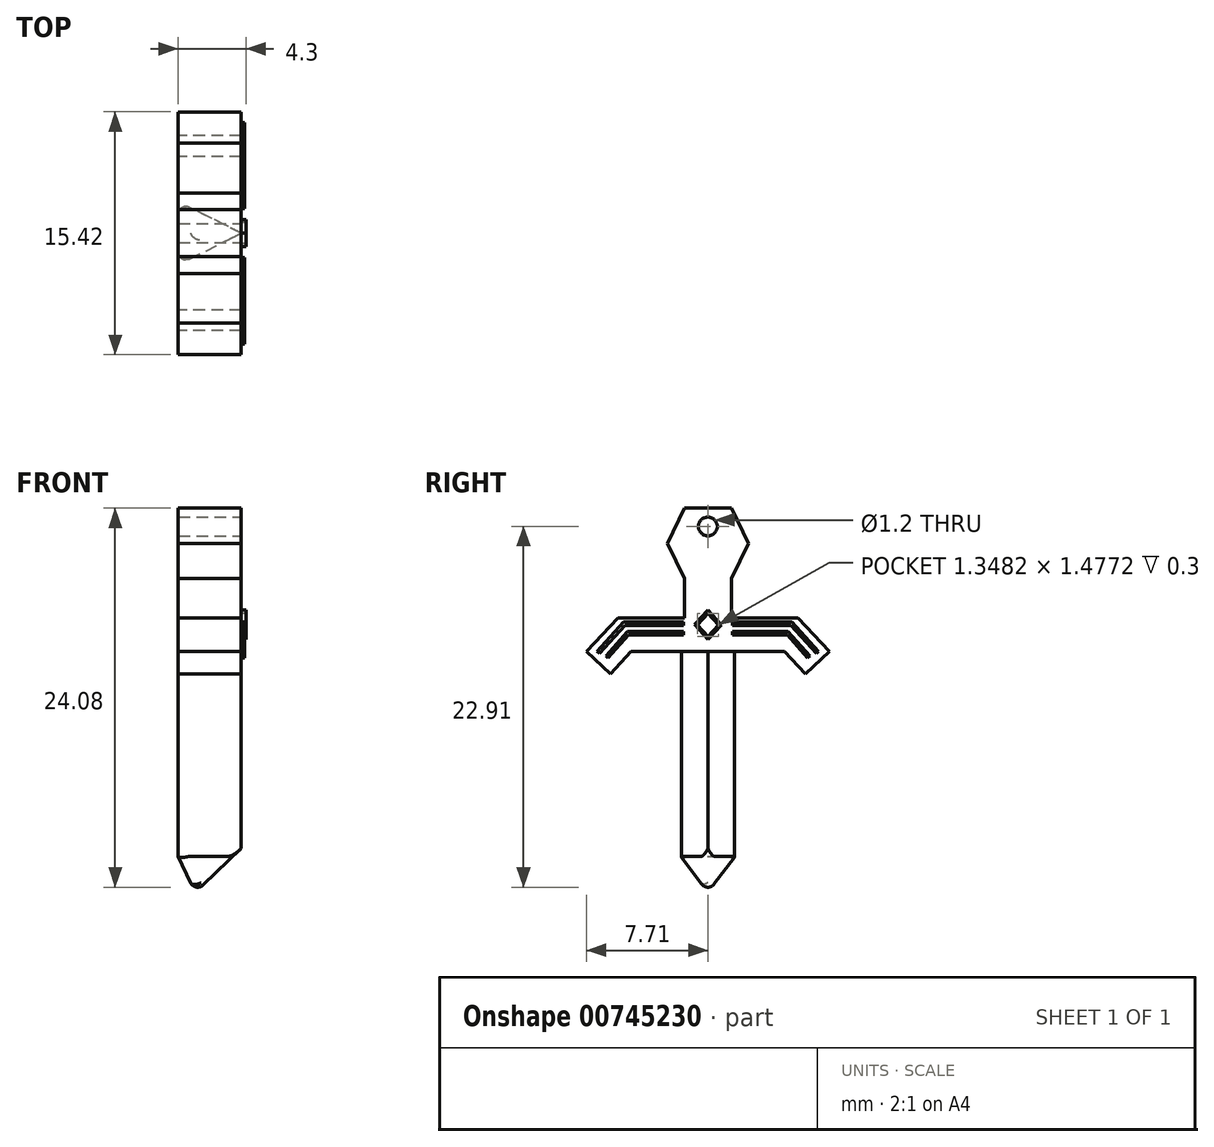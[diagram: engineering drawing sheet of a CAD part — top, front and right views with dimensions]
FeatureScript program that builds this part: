
annotation { "Feature Type Name" : "Feature", "Feature Type Description" : "" }
export const myFeature = defineFeature(function(context is Context, id is Id, definition is map)
    precondition{}
    {
        {
            var Q0;
            Q0=qCreatedBy(makeId("Right.planeOp"),FACE);
            var sketch = newSketch(context, id + "F0", { "sketchPlane" : qUnion([Q0])});
            skLineSegment(sketch, "E0", {"start": v(-3.3, 24.4) * mm, "end": v(1.49, 24.4) * mm});
            skLineSegment(sketch, "E1", {"start": v(1.49, 24.4) * mm, "end": v(2.56, 22.15) * mm});
            skLineSegment(sketch, "E2", {"start": v(2.56, 22.15) * mm, "end": v(1.49, 19.92) * mm});
            skLineSegment(sketch, "E3", {"start": v(1.49, 19.92) * mm, "end": v(1.49, 17.4) * mm});
            skLineSegment(sketch, "E4", {"start": v(1.49, 17.4) * mm, "end": v(5.72, 17.4) * mm});
            skLineSegment(sketch, "E5", {"start": v(5.72, 17.4) * mm, "end": v(7.7, 15.27) * mm});
            skLineSegment(sketch, "E6", {"start": v(7.7, 15.27) * mm, "end": v(6.2, 13.86) * mm});
            skLineSegment(sketch, "E7", {"start": v(6.2, 13.86) * mm, "end": v(4.87, 15.27) * mm});
            skLineSegment(sketch, "E8", {"start": v(4.87, 15.27) * mm, "end": v(1.49, 15.27) * mm});
            skLineSegment(sketch, "E9.MirrorCS", {"start": v(-1.49, 24.4) * mm, "end": v(-2.56, 22.15) * mm});
            skLineSegment(sketch, "E10.MirrorCS", {"start": v(-2.56, 22.15) * mm, "end": v(-1.49, 19.92) * mm});
            skLineSegment(sketch, "E11.MirrorCS", {"start": v(-1.49, 19.92) * mm, "end": v(-1.49, 17.4) * mm});
            skLineSegment(sketch, "E12.MirrorCS", {"start": v(-1.49, 17.4) * mm, "end": v(-5.72, 17.4) * mm});
            skLineSegment(sketch, "E13.MirrorCS", {"start": v(-5.72, 17.4) * mm, "end": v(-7.7, 15.27) * mm});
            skLineSegment(sketch, "E14.MirrorCS", {"start": v(-7.7, 15.27) * mm, "end": v(-6.2, 13.86) * mm});
            skLineSegment(sketch, "E15.MirrorCS", {"start": v(-6.2, 13.86) * mm, "end": v(-4.87, 15.27) * mm});
            skLineSegment(sketch, "E16.MirrorCS", {"start": v(-4.87, 15.27) * mm, "end": v(-1.49, 15.27) * mm});
            skLineSegment(sketch, "E17", {"start": v(-1.49, 15.27) * mm, "end": v(1.49, 15.27) * mm});
            skSolve(sketch);
        }
        {
            var Q0;
            Q0 = qSketchRegion(id + "F0", true);
            extrude(context, id + "F1", {"entities" : qUnion([Q0]), "depth" : 4 * mm, "offsetDistance" : 25 * mm});
        }
        {
            var Q0;
            Q0=makeQuery(id+"F1.opExtrude","SWEPT_FACE",FACE,{"disambiguationData":[OSD([sQuery(id+"F0.wireOp",EDGE,"E8"),sQuery(id+"F0.wireOp",EDGE,"E16.MirrorCS"),sQuery(id+"F0.wireOp",EDGE,"E17")])]});
            var sketch = newSketch(context, id + "F2", { "sketchPlane" : qUnion([Q0])});
            skLineSegment(sketch, "E18", {"start": v(0, 0) * mm, "end": v(0, 2) * mm});
            skLineSegment(sketch, "E19", {"start": v(0, 2) * mm, "end": v(4, 0) * mm});
            skLineSegment(sketch, "E20", {"start": v(4, 0) * mm, "end": v(0, -2) * mm});
            skLineSegment(sketch, "E21", {"start": v(0, -2) * mm, "end": v(0, 0) * mm});
            skSolve(sketch);
        }
        {
            var Q0;
            Q0=makeQuery(id+"F2.imprint","IMPRINT",FACE,{"disambiguationData":[TD([[makeQuery(id+"F2.imprint","IMPRINT",EDGE,{"derivedFrom":sQuery(id+"F2.wireOp",EDGE,"E18")}),1.0]])]});
            extrude(context, id + "F3", {"entities" : qUnion([Q0]), "operationType" : NewBodyOperationType.ADD, "depth" : 13 * mm, "offsetDistance" : 25 * mm});
        }
        {
            var Q0;
            Q0=makeQuery(id+"F1.opExtrude","CAP_FACE",FACE,{"disambiguationData":[OSD([sQuery(id+"F0.wireOp",EDGE,"E0"),sQuery(id+"F0.wireOp",EDGE,"E1"),sQuery(id+"F0.wireOp",EDGE,"E2"),sQuery(id+"F0.wireOp",EDGE,"E3"),sQuery(id+"F0.wireOp",EDGE,"E4"),sQuery(id+"F0.wireOp",EDGE,"E5"),sQuery(id+"F0.wireOp",EDGE,"E6"),sQuery(id+"F0.wireOp",EDGE,"E7"),sQuery(id+"F0.wireOp",EDGE,"E8"),sQuery(id+"F0.wireOp",EDGE,"E9.MirrorCS"),sQuery(id+"F0.wireOp",EDGE,"E10.MirrorCS"),sQuery(id+"F0.wireOp",EDGE,"E11.MirrorCS"),sQuery(id+"F0.wireOp",EDGE,"E12.MirrorCS"),sQuery(id+"F0.wireOp",EDGE,"E13.MirrorCS"),sQuery(id+"F0.wireOp",EDGE,"E14.MirrorCS"),sQuery(id+"F0.wireOp",EDGE,"E15.MirrorCS"),sQuery(id+"F0.wireOp",EDGE,"E16.MirrorCS"),sQuery(id+"F0.wireOp",EDGE,"E17")])],"isStart":false});
            var sketch = newSketch(context, id + "F4", { "sketchPlane" : qUnion([Q0])});
            skCircle(sketch, "E22", {"center": v(0, 23.22) * mm, "radius": 0.6 * mm});
            skSolve(sketch);
        }
        {
            var Q0;
            Q0=makeQuery(id+"F4.imprint","IMPRINT",FACE,{"disambiguationData":[TD([[makeQuery(id+"F4.imprint","IMPRINT",EDGE,{"derivedFrom":sQuery(id+"F4.wireOp",EDGE,"E22")}),1.0]])]});
            extrude(context, id + "F5", {"entities" : qUnion([Q0]), "operationType" : NewBodyOperationType.REMOVE, "oppositeDirection" : true, "depth" : 25 * mm, "offsetDistance" : 25 * mm});
        }
        {
            var Q0;
            Q0=makeQuery(id+"F3.opExtrude","CAP_FACE",FACE,{"disambiguationData":[OSD([sQuery(id+"F2.wireOp",EDGE,"E18"),sQuery(id+"F2.wireOp",EDGE,"E19"),sQuery(id+"F2.wireOp",EDGE,"E20"),sQuery(id+"F2.wireOp",EDGE,"E21")])],"isStart":false});
            var sketch = newSketch(context, id + "F6", { "sketchPlane" : qUnion([Q0])});
            skLineSegment(sketch, "E23", {"start": v(0, 0) * mm, "end": v(0, 2) * mm});
            skLineSegment(sketch, "E24", {"start": v(0, 2) * mm, "end": v(4, 0) * mm});
            skLineSegment(sketch, "E25", {"start": v(4, 0) * mm, "end": v(0, -2) * mm});
            skLineSegment(sketch, "E26", {"start": v(0, -2) * mm, "end": v(0, 0) * mm});
            skSolve(sketch);
        }
        {
            var Q0;
            Q0 = qSketchRegion(id + "F6", true);
            extrude(context, id + "F7", {"entities" : qUnion([Q0]), "operationType" : NewBodyOperationType.ADD, "depth" : 2.8 * mm, "offsetDistance" : 25 * mm, "hasDraft" : true, "draftAngle" : 25 * degree, "draftPullDirection" : true});
        }
        {
            var Q0;
            Q0=makeQuery(id+"F1.opExtrude","CAP_FACE",FACE,{"disambiguationData":[OSD([sQuery(id+"F0.wireOp",EDGE,"E0"),sQuery(id+"F0.wireOp",EDGE,"E1"),sQuery(id+"F0.wireOp",EDGE,"E2"),sQuery(id+"F0.wireOp",EDGE,"E3"),sQuery(id+"F0.wireOp",EDGE,"E4"),sQuery(id+"F0.wireOp",EDGE,"E5"),sQuery(id+"F0.wireOp",EDGE,"E6"),sQuery(id+"F0.wireOp",EDGE,"E7"),sQuery(id+"F0.wireOp",EDGE,"E8"),sQuery(id+"F0.wireOp",EDGE,"E9.MirrorCS"),sQuery(id+"F0.wireOp",EDGE,"E10.MirrorCS"),sQuery(id+"F0.wireOp",EDGE,"E11.MirrorCS"),sQuery(id+"F0.wireOp",EDGE,"E12.MirrorCS"),sQuery(id+"F0.wireOp",EDGE,"E13.MirrorCS"),sQuery(id+"F0.wireOp",EDGE,"E14.MirrorCS"),sQuery(id+"F0.wireOp",EDGE,"E15.MirrorCS"),sQuery(id+"F0.wireOp",EDGE,"E16.MirrorCS"),sQuery(id+"F0.wireOp",EDGE,"E17")])],"isStart":false});
            var sketch = newSketch(context, id + "F8", { "sketchPlane" : qUnion([Q0])});
            skLineSegment(sketch, "E27", {"start": v(-1.55, 17.02) * mm, "end": v(-1.55, 16.92) * mm});
            skLineSegment(sketch, "E28", {"start": v(-1.55, 16.92) * mm, "end": v(-5.28, 16.92) * mm});
            skLineSegment(sketch, "E29", {"start": v(-5.28, 16.92) * mm, "end": v(-6.88, 15.16) * mm});
            skLineSegment(sketch, "E30", {"start": v(-6.88, 15.16) * mm, "end": v(-7.03, 15.3) * mm});
            skLineSegment(sketch, "E31", {"start": v(-7.03, 15.3) * mm, "end": v(-5.35, 17.14) * mm});
            skLineSegment(sketch, "E32", {"start": v(-5.35, 17.14) * mm, "end": v(-1.55, 17.14) * mm});
            skLineSegment(sketch, "E33", {"start": v(-1.55, 17.14) * mm, "end": v(-1.55, 17.02) * mm});
            skLineSegment(sketch, "E34", {"start": v(-1.55, 16.46) * mm, "end": v(-1.55, 16.33) * mm});
            skLineSegment(sketch, "E35", {"start": v(-1.55, 16.33) * mm, "end": v(-5.05, 16.33) * mm});
            skLineSegment(sketch, "E36", {"start": v(-5.05, 16.33) * mm, "end": v(-6.34, 14.87) * mm});
            skLineSegment(sketch, "E37", {"start": v(-6.34, 14.87) * mm, "end": v(-6.47, 15) * mm});
            skLineSegment(sketch, "E38", {"start": v(-6.47, 15) * mm, "end": v(-5.1, 16.54) * mm});
            skLineSegment(sketch, "E39", {"start": v(-5.1, 16.54) * mm, "end": v(-1.55, 16.54) * mm});
            skLineSegment(sketch, "E40", {"start": v(-1.55, 16.54) * mm, "end": v(-1.55, 16.46) * mm});
            skLineSegment(sketch, "E41.MirrorCS", {"start": v(5.1, 16.54) * mm, "end": v(1.55, 16.54) * mm});
            skLineSegment(sketch, "E42.MirrorCS", {"start": v(1.55, 16.33) * mm, "end": v(5.05, 16.33) * mm});
            skLineSegment(sketch, "E43.MirrorCS", {"start": v(1.55, 16.46) * mm, "end": v(1.55, 16.33) * mm});
            skLineSegment(sketch, "E44.MirrorCS", {"start": v(1.55, 16.54) * mm, "end": v(1.55, 16.46) * mm});
            skLineSegment(sketch, "E45.MirrorCS", {"start": v(5.05, 16.33) * mm, "end": v(6.34, 14.87) * mm});
            skLineSegment(sketch, "E46.MirrorCS", {"start": v(6.47, 15) * mm, "end": v(5.1, 16.54) * mm});
            skLineSegment(sketch, "E47.MirrorCS", {"start": v(6.34, 14.87) * mm, "end": v(6.47, 15) * mm});
            skLineSegment(sketch, "E48.MirrorCS", {"start": v(6.88, 15.16) * mm, "end": v(7.03, 15.3) * mm});
            skLineSegment(sketch, "E49.MirrorCS", {"start": v(5.28, 16.92) * mm, "end": v(6.88, 15.16) * mm});
            skLineSegment(sketch, "E50.MirrorCS", {"start": v(7.03, 15.3) * mm, "end": v(5.35, 17.14) * mm});
            skLineSegment(sketch, "E51.MirrorCS", {"start": v(1.55, 16.92) * mm, "end": v(5.28, 16.92) * mm});
            skLineSegment(sketch, "E52.MirrorCS", {"start": v(5.35, 17.14) * mm, "end": v(1.55, 17.14) * mm});
            skLineSegment(sketch, "E53.MirrorCS", {"start": v(1.55, 17.14) * mm, "end": v(1.55, 17.02) * mm});
            skLineSegment(sketch, "E54.MirrorCS", {"start": v(1.55, 17.02) * mm, "end": v(1.55, 16.92) * mm});
            skSolve(sketch);
        }
        {
            var Q0;
            Q0 = qSketchRegion(id + "F8", true);
            extrude(context, id + "F9", {"entities" : qUnion([Q0]), "operationType" : NewBodyOperationType.ADD, "depth" : 0.2 * mm, "offsetDistance" : 25 * mm});
        }
        {
            var Q0;
            Q0=makeQuery(id+"F1.opExtrude","CAP_FACE",FACE,{"disambiguationData":[OSD([sQuery(id+"F0.wireOp",EDGE,"E0"),sQuery(id+"F0.wireOp",EDGE,"E1"),sQuery(id+"F0.wireOp",EDGE,"E2"),sQuery(id+"F0.wireOp",EDGE,"E3"),sQuery(id+"F0.wireOp",EDGE,"E4"),sQuery(id+"F0.wireOp",EDGE,"E5"),sQuery(id+"F0.wireOp",EDGE,"E6"),sQuery(id+"F0.wireOp",EDGE,"E7"),sQuery(id+"F0.wireOp",EDGE,"E8"),sQuery(id+"F0.wireOp",EDGE,"E9.MirrorCS"),sQuery(id+"F0.wireOp",EDGE,"E10.MirrorCS"),sQuery(id+"F0.wireOp",EDGE,"E11.MirrorCS"),sQuery(id+"F0.wireOp",EDGE,"E12.MirrorCS"),sQuery(id+"F0.wireOp",EDGE,"E13.MirrorCS"),sQuery(id+"F0.wireOp",EDGE,"E14.MirrorCS"),sQuery(id+"F0.wireOp",EDGE,"E15.MirrorCS"),sQuery(id+"F0.wireOp",EDGE,"E16.MirrorCS"),sQuery(id+"F0.wireOp",EDGE,"E17")])],"isStart":false});
            var sketch = newSketch(context, id + "F10", { "sketchPlane" : qUnion([Q0])});
            skLineSegment(sketch, "E55", {"start": v(0, 17.71) * mm, "end": v(-0.67, 16.97) * mm});
            skLineSegment(sketch, "E56", {"start": v(-0.67, 16.97) * mm, "end": v(0, 16.23) * mm});
            skLineSegment(sketch, "E57.MirrorCS", {"start": v(0, 17.71) * mm, "end": v(0.67, 16.97) * mm});
            skLineSegment(sketch, "E58.MirrorCS", {"start": v(0.67, 16.97) * mm, "end": v(0, 16.23) * mm});
            skLineSegment(sketch, "E59", {"start": v(0, 17.91) * mm, "end": v(-0.86, 17) * mm});
            skLineSegment(sketch, "E60", {"start": v(-0.86, 17) * mm, "end": v(0, 16.03) * mm});
            skLineSegment(sketch, "E61", {"start": v(0, 16.03) * mm, "end": v(0.86, 16.97) * mm});
            skLineSegment(sketch, "E62", {"start": v(0.86, 16.97) * mm, "end": v(0, 17.91) * mm});
            skSolve(sketch);
        }
        {
            var Q0;
            Q0 = qSketchRegion(id + "F10", true);
            extrude(context, id + "F11", {"entities" : qUnion([Q0]), "operationType" : NewBodyOperationType.ADD, "depth" : 0.3 * mm, "offsetDistance" : 25 * mm});
        }
        {
            var Q0;
            Q0=makeQuery(id+"F3.opExtrude","SWEPT_EDGE",EDGE,{"disambiguationData":[OSD([sQuery(id+"F0.wireOp",EDGE,"E8"),sQuery(id+"F0.wireOp",EDGE,"E16.MirrorCS"),sQuery(id+"F0.wireOp",EDGE,"E17"),sQuery(id+"F2.wireOp",EDGE,"E20"),sQuery(id+"F2.wireOp",EDGE,"E21")])]});
            fillet(context, id + "F12", {"entities" : qUnion([Q0]), "radius" : 0.5 * mm, "tangentPropagation" : true, "allowEdgeOverflow" : false});
        }
        {
            var Q0;
            Q0=makeQuery(id+"F3.opExtrude","SWEPT_EDGE",EDGE,{"disambiguationData":[OSD([sQuery(id+"F0.wireOp",EDGE,"E8"),sQuery(id+"F0.wireOp",EDGE,"E16.MirrorCS"),sQuery(id+"F0.wireOp",EDGE,"E17"),sQuery(id+"F2.wireOp",EDGE,"E18"),sQuery(id+"F2.wireOp",EDGE,"E19")])]});
            fillet(context, id + "F13", {"entities" : qUnion([Q0]), "radius" : 0.5 * mm, "tangentPropagation" : true, "allowEdgeOverflow" : false});
        }
        {
            var Q0;
            Q0=makeQuery(id+"F7.opExtrude","SWEPT_EDGE",EDGE,{"disambiguationData":[OSD([sQuery(id+"F6.wireOp",EDGE,"E23"),sQuery(id+"F6.wireOp",EDGE,"E24")])]});
            fillet(context, id + "F14", {"entities" : qUnion([Q0]), "radius" : 0.5 * mm, "tangentPropagation" : true, "allowEdgeOverflow" : false});
        }
        {
            var Q0;
            Q0=makeQuery(id+"F7.opExtrude","SWEPT_EDGE",EDGE,{"disambiguationData":[OSD([sQuery(id+"F6.wireOp",EDGE,"E25"),sQuery(id+"F6.wireOp",EDGE,"E26")])]});
            fillet(context, id + "F15", {"entities" : qUnion([Q0]), "radius" : 0.5 * mm, "tangentPropagation" : true, "allowEdgeOverflow" : false});
        }
    });
